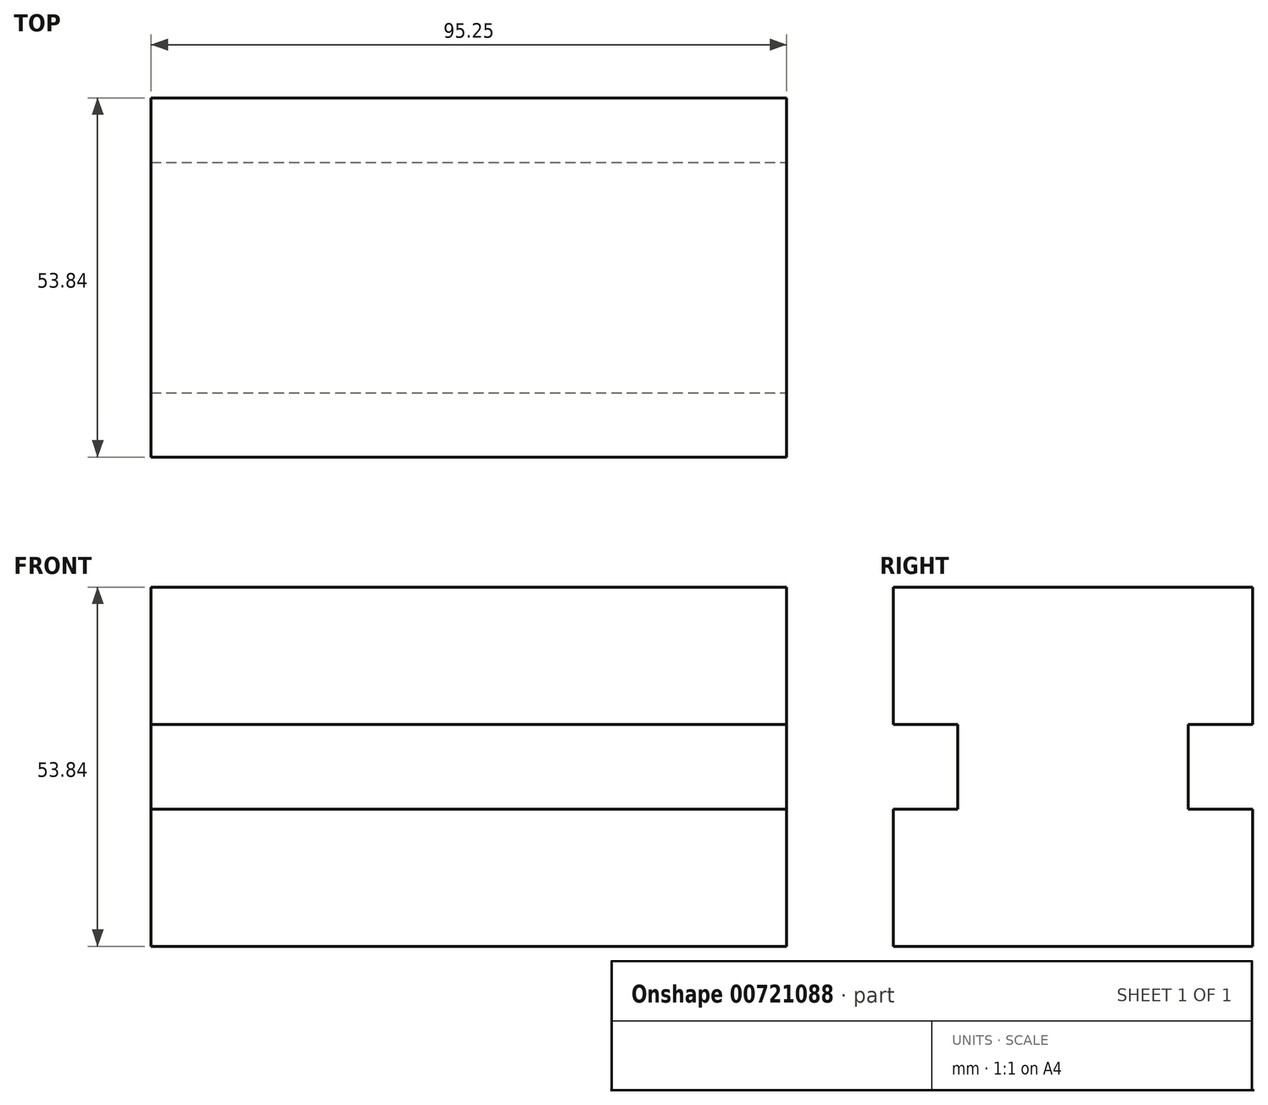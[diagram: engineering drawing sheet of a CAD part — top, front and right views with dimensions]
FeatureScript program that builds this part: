
annotation { "Feature Type Name" : "Feature", "Feature Type Description" : "" }
export const myFeature = defineFeature(function(context is Context, id is Id, definition is map)
    precondition{}
    {
        {
            var Q0;
            Q0=qCreatedBy(makeId("Right.planeOp"),FACE);
            var sketch = newSketch(context, id + "F0", { "sketchPlane" : qUnion([Q0])});
            skLineSegment(sketch, "E0.bottom", {"start": v(26.92, -26.92) * mm, "end": v(-26.92, -26.92) * mm});
            skLineSegment(sketch, "E0.top", {"start": v(26.92, 26.92) * mm, "end": v(-26.92, 26.92) * mm});
            skLineSegment(sketch, "E0.left", {"start": v(26.92, -26.92) * mm, "end": v(26.92, -6.35) * mm});
            skLineSegment(sketch, "E0.right", {"start": v(-26.92, -26.92) * mm, "end": v(-26.92, -6.35) * mm});
            skPoint(sketch, "E0.middle", {"position": v(0, 0) * mm});
            skLineSegment(sketch, "E1.bottom", {"start": v(-26.92, 6.35) * mm, "end": v(-17.27, 6.35) * mm});
            skLineSegment(sketch, "E1.top", {"start": v(-26.92, -6.35) * mm, "end": v(-17.27, -6.35) * mm});
            skLineSegment(sketch, "E1.right", {"start": v(-17.27, 6.35) * mm, "end": v(-17.27, -6.35) * mm});
            skLineSegment(sketch, "E2", {"start": v(0, 29.65) * mm, "end": v(0, -30.12) * mm, "construction": true});
            skLineSegment(sketch, "E3.MirrorCS", {"start": v(26.92, 6.35) * mm, "end": v(17.27, 6.35) * mm});
            skLineSegment(sketch, "E4.MirrorCS", {"start": v(17.27, 6.35) * mm, "end": v(17.27, -6.35) * mm});
            skLineSegment(sketch, "E5.MirrorCS", {"start": v(26.92, -6.35) * mm, "end": v(17.27, -6.35) * mm});
            skLineSegment(sketch, "E6.trimOffspring", {"start": v(-26.92, 6.35) * mm, "end": v(-26.92, 26.92) * mm});
            skLineSegment(sketch, "E7.trimOffspring", {"start": v(26.92, 6.35) * mm, "end": v(26.92, 26.92) * mm});
            skSolve(sketch);
        }
        {
            var Q0;
            Q0=makeQuery(id+"F0.imprint","IMPRINT",FACE,{"disambiguationData":[TD([[makeQuery(id+"F0.imprint","IMPRINT",EDGE,{"derivedFrom":sQuery(id+"F0.wireOp",EDGE,"E0.bottom")}),-1.0]])]});
            extrude(context, id + "F1", {"entities" : qUnion([Q0]), "oppositeDirection" : true, "depth" : 95.25 * mm, "offsetDistance" : 25.4 * mm});
        }
    });
